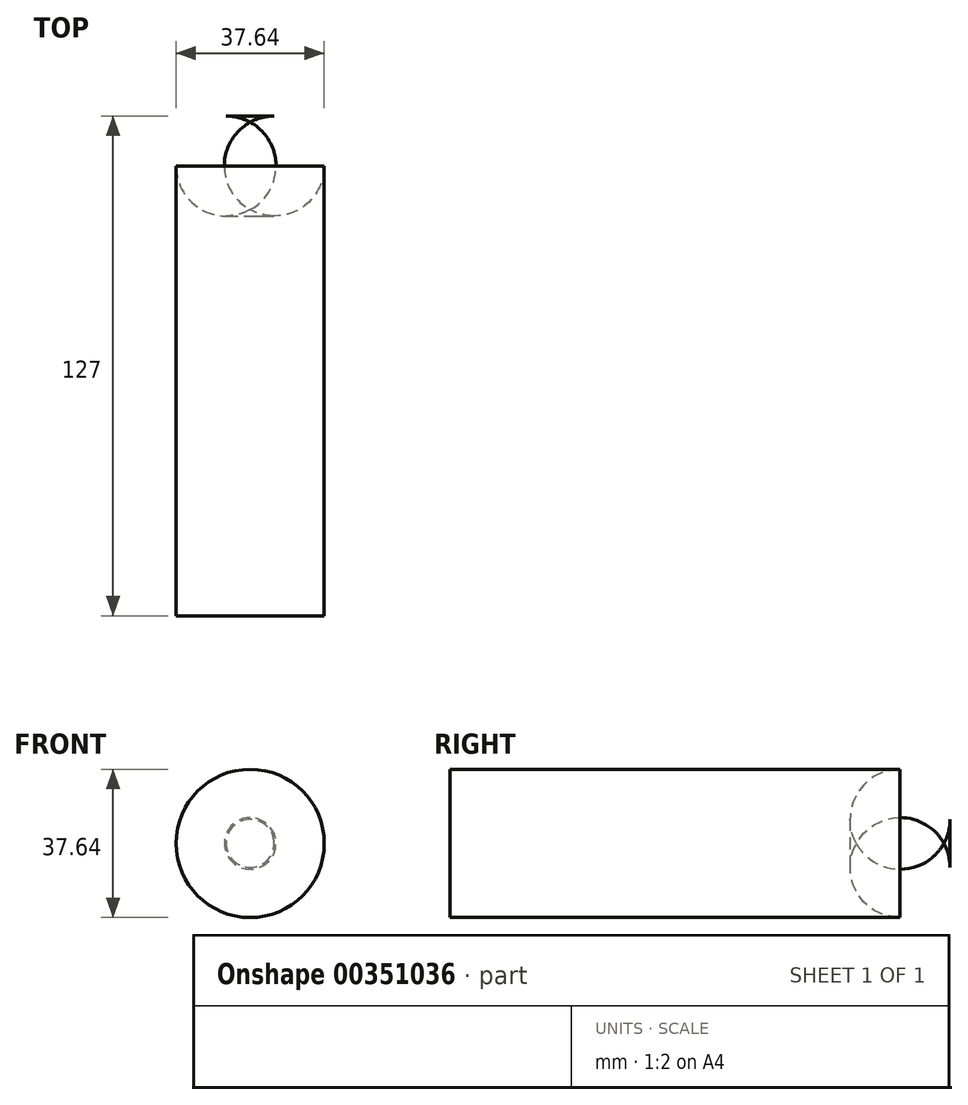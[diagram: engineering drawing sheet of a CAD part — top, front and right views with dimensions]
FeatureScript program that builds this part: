
annotation { "Feature Type Name" : "Feature", "Feature Type Description" : "" }
export const myFeature = defineFeature(function(context is Context, id is Id, definition is map)
    precondition{}
    {
        {
            var Q0;
            Q0=qCreatedBy(makeId("Front.planeOp"),FACE);
            var sketch = newSketch(context, id + "F0", { "sketchPlane" : qUnion([Q0])});
            skCircle(sketch, "E0", {"center": v(0, 0) * mm, "radius": 18.82 * mm});
            skSolve(sketch);
        }
        {
            var Q0;
            Q0=makeQuery(id+"F0.imprint","IMPRINT",FACE,{"disambiguationData":[TD([[makeQuery(id+"F0.imprint","IMPRINT",EDGE,{"derivedFrom":sQuery(id+"F0.wireOp",EDGE,"E0")}),1.0]])]});
            extrude(context, id + "F1", {"entities" : qUnion([Q0]), "depth" : 127 * mm});
        }
        {
            var Q0;
            Q0=makeQuery(id+"F1.opExtrude","CAP_EDGE",EDGE,{"disambiguationData":[OSD([sQuery(id+"F0.wireOp",EDGE,"E0")])],"isStart":true});
            fillet(context, id + "F2", {"entities" : qUnion([Q0]), "radius" : 12.7 * mm, "tangentPropagation" : true, "allowEdgeOverflow" : false});
        }
    });
